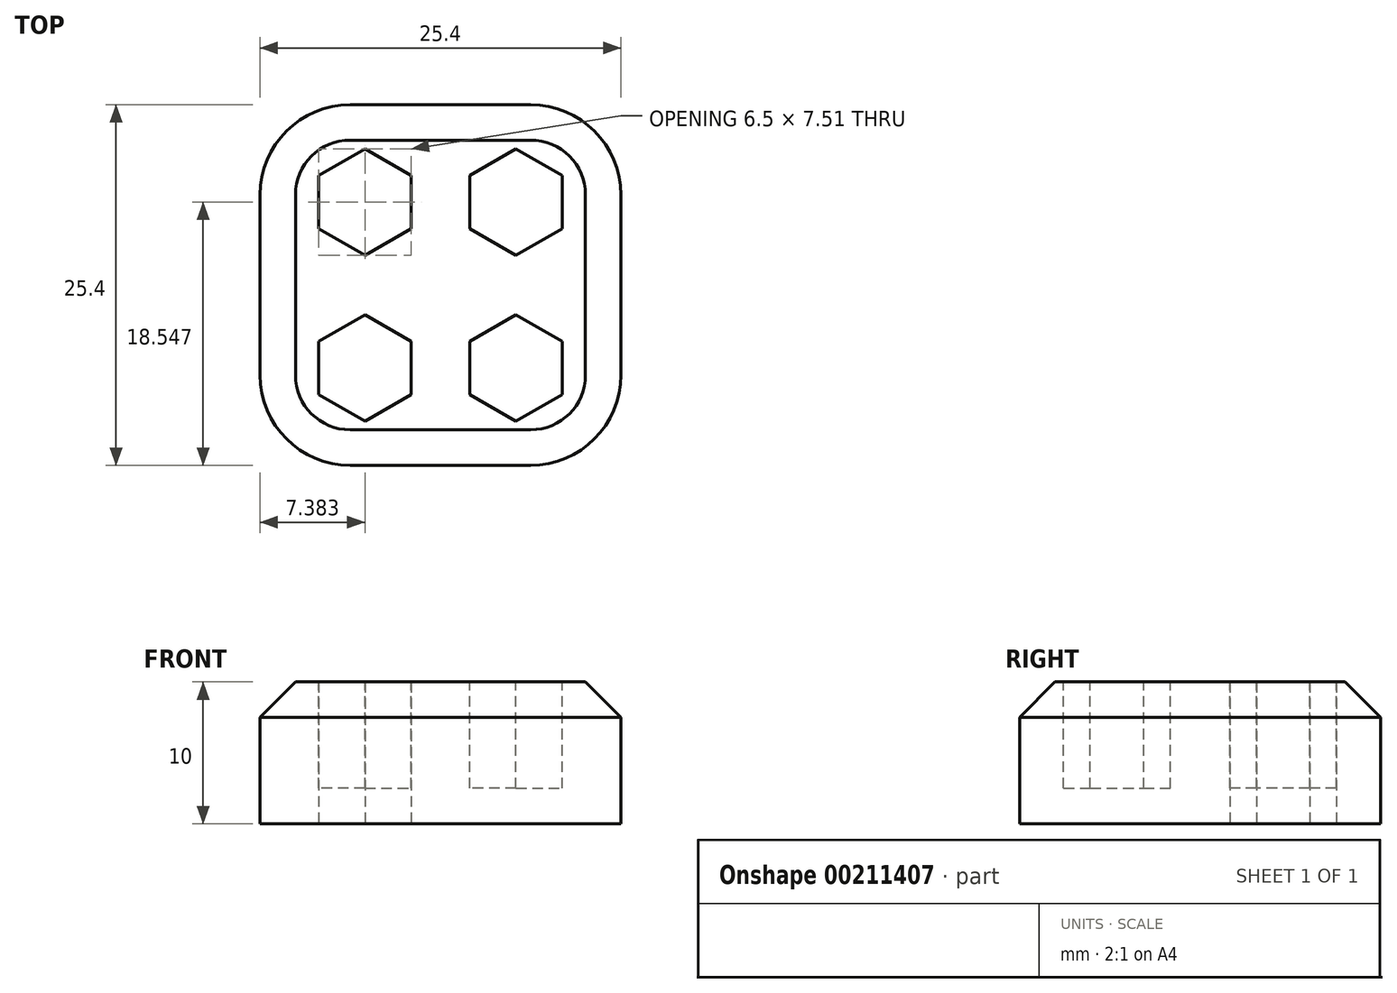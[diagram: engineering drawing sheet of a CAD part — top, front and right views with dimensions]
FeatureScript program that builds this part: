
annotation { "Feature Type Name" : "Feature", "Feature Type Description" : "" }
export const myFeature = defineFeature(function(context is Context, id is Id, definition is map)
    precondition{}
    {
        {
            var Q0;
            Q0=qCreatedBy(makeId("Top.planeOp"),FACE);
            var sketch = newSketch(context, id + "F0", { "sketchPlane" : qUnion([Q0])});
            skLineSegment(sketch, "E0.bottom", {"start": v(-12.7, 12.7) * mm, "end": v(12.7, 12.7) * mm});
            skLineSegment(sketch, "E0.top", {"start": v(-12.7, -12.7) * mm, "end": v(12.7, -12.7) * mm});
            skLineSegment(sketch, "E0.left", {"start": v(-12.7, 12.7) * mm, "end": v(-12.7, -12.7) * mm});
            skLineSegment(sketch, "E0.right", {"start": v(12.7, 12.7) * mm, "end": v(12.7, -12.7) * mm});
            skLineSegment(sketch, "E1", {"start": v(-12.7, 12.7) * mm, "end": v(12.7, -12.7) * mm, "construction": true});
            skLineSegment(sketch, "E2", {"start": v(-12.7, 5.85) * mm, "end": v(12.7, 5.85) * mm, "construction": true});
            skLineSegment(sketch, "E3", {"start": v(-5.32, 12.7) * mm, "end": v(-5.32, -12.7) * mm, "construction": true});
            skCircle(sketch, "E4.cCircle", {"center": v(-5.32, 5.85) * mm, "radius": 3.25 * mm, "construction": true});
            skLineSegment(sketch, "E4.0", {"start": v(-2.07, 7.72) * mm, "end": v(-2.07, 3.97) * mm});
            skLineSegment(sketch, "E4.1", {"start": v(-2.07, 3.97) * mm, "end": v(-5.32, 2.1) * mm});
            skLineSegment(sketch, "E4.2", {"start": v(-5.32, 2.1) * mm, "end": v(-8.57, 3.97) * mm});
            skLineSegment(sketch, "E4.3", {"start": v(-8.57, 3.97) * mm, "end": v(-8.57, 7.72) * mm});
            skLineSegment(sketch, "E4.4", {"start": v(-8.57, 7.72) * mm, "end": v(-5.32, 9.6) * mm});
            skLineSegment(sketch, "E4.5", {"start": v(-5.32, 9.6) * mm, "end": v(-2.07, 7.72) * mm});
            skPoint(sketch, "E4.0.midPoint", {"position": v(-2.07, 5.85) * mm});
            skCircle(sketch, "E5.MirrorC", {"center": v(5.32, 5.85) * mm, "radius": 3.25 * mm, "construction": true});
            skLineSegment(sketch, "E6.MirrorCS", {"start": v(2.07, 7.72) * mm, "end": v(2.07, 3.97) * mm});
            skLineSegment(sketch, "E7.MirrorCS", {"start": v(2.07, 3.97) * mm, "end": v(5.32, 2.1) * mm});
            skLineSegment(sketch, "E8.MirrorCS", {"start": v(5.32, 2.1) * mm, "end": v(8.57, 3.97) * mm});
            skLineSegment(sketch, "E9.MirrorCS", {"start": v(8.57, 3.97) * mm, "end": v(8.57, 7.72) * mm});
            skLineSegment(sketch, "E10.MirrorCS", {"start": v(5.32, 9.6) * mm, "end": v(2.07, 7.72) * mm});
            skLineSegment(sketch, "E11.MirrorCS", {"start": v(8.57, 7.72) * mm, "end": v(5.32, 9.6) * mm});
            skPoint(sketch, "E12.MirrorP", {"position": v(2.07, 5.85) * mm});
            skLineSegment(sketch, "E13.MirrorCS", {"start": v(8.57, -3.97) * mm, "end": v(8.57, -7.72) * mm});
            skPoint(sketch, "E14.MirrorP", {"position": v(-2.07, -5.85) * mm});
            skLineSegment(sketch, "E15.MirrorCS", {"start": v(5.32, -2.1) * mm, "end": v(8.57, -3.97) * mm});
            skCircle(sketch, "E16.MirrorC", {"center": v(-5.32, -5.85) * mm, "radius": 3.25 * mm, "construction": true});
            skLineSegment(sketch, "E17.MirrorCS", {"start": v(-2.07, -7.72) * mm, "end": v(-2.07, -3.97) * mm});
            skLineSegment(sketch, "E18.MirrorCS", {"start": v(-2.07, -3.97) * mm, "end": v(-5.32, -2.1) * mm});
            skLineSegment(sketch, "E19.MirrorCS", {"start": v(-5.32, -2.1) * mm, "end": v(-8.57, -3.97) * mm});
            skPoint(sketch, "E20.MirrorP", {"position": v(2.07, -5.85) * mm});
            skLineSegment(sketch, "E21.MirrorCS", {"start": v(2.07, -3.97) * mm, "end": v(5.32, -2.1) * mm});
            skLineSegment(sketch, "E22.MirrorCS", {"start": v(2.07, -7.72) * mm, "end": v(2.07, -3.97) * mm});
            skLineSegment(sketch, "E23.MirrorCS", {"start": v(-8.57, -3.97) * mm, "end": v(-8.57, -7.72) * mm});
            skLineSegment(sketch, "E24.MirrorCS", {"start": v(-5.32, -9.6) * mm, "end": v(-2.07, -7.72) * mm});
            skLineSegment(sketch, "E25.MirrorCS", {"start": v(8.57, -7.72) * mm, "end": v(5.32, -9.6) * mm});
            skLineSegment(sketch, "E26.MirrorCS", {"start": v(5.32, -9.6) * mm, "end": v(2.07, -7.72) * mm});
            skLineSegment(sketch, "E27.MirrorCS", {"start": v(-8.57, -7.72) * mm, "end": v(-5.32, -9.6) * mm});
            skCircle(sketch, "E28.MirrorC", {"center": v(5.32, -5.85) * mm, "radius": 3.25 * mm, "construction": true});
            skSolve(sketch);
        }
        {
            var Q0;
            Q0=makeQuery(id+"F0.imprint","IMPRINT",FACE,{"disambiguationData":[TD([[makeQuery(id+"F0.imprint","IMPRINT",EDGE,{"derivedFrom":sQuery(id+"F0.wireOp",EDGE,"E0.bottom")}),-1.0]])]});
            var Q1;
            Q1=makeQuery(id+"F0.imprint","IMPRINT",FACE,{"disambiguationData":[TD([[makeQuery(id+"F0.imprint","IMPRINT",EDGE,{"derivedFrom":sQuery(id+"F0.wireOp",EDGE,"E24.MirrorCS")}),1.0]])]});
            var Q2;
            Q2=makeQuery(id+"F0.imprint","IMPRINT",FACE,{"disambiguationData":[TD([[makeQuery(id+"F0.imprint","IMPRINT",EDGE,{"derivedFrom":sQuery(id+"F0.wireOp",EDGE,"E10.MirrorCS")}),1.0]])]});
            var Q3;
            Q3=makeQuery(id+"F0.imprint","IMPRINT",FACE,{"disambiguationData":[TD([[makeQuery(id+"F0.imprint","IMPRINT",EDGE,{"derivedFrom":sQuery(id+"F0.wireOp",EDGE,"E13.MirrorCS")}),-1.0]])]});
            var Q4;
            Q4=makeQuery(id+"F0.imprint","IMPRINT",FACE,{"disambiguationData":[TD([[makeQuery(id+"F0.imprint","IMPRINT",EDGE,{"derivedFrom":sQuery(id+"F0.wireOp",EDGE,"E4.5")}),-1.0]])]});
            extrude(context, id + "F1", {"entities" : qUnion([Q0, Q1, Q2, Q3, Q4]), "depth" : 10 * mm});
        }
        {
            var Q0;
            Q0=makeQuery(id+"F1.opExtrude","CAP_FACE",FACE,{"disambiguationData":[OSD([sQuery(id+"F0.wireOp",EDGE,"E0.bottom"),sQuery(id+"F0.wireOp",EDGE,"E0.top"),sQuery(id+"F0.wireOp",EDGE,"E0.left"),sQuery(id+"F0.wireOp",EDGE,"E0.right")])],"isStart":false});
            var sketch = newSketch(context, id + "F2", { "sketchPlane" : qUnion([Q0])});
            skLineSegment(sketch, "E29.0", {"start": v(-8.57, 7.72) * mm, "end": v(-5.32, 9.6) * mm});
            skLineSegment(sketch, "E30.0", {"start": v(-8.57, 3.97) * mm, "end": v(-8.57, 7.72) * mm});
            skLineSegment(sketch, "E31.0", {"start": v(-5.32, 2.1) * mm, "end": v(-8.57, 3.97) * mm});
            skLineSegment(sketch, "E32.0", {"start": v(-5.32, 9.6) * mm, "end": v(-2.07, 7.72) * mm});
            skLineSegment(sketch, "E33.0", {"start": v(-2.07, 7.72) * mm, "end": v(-2.07, 3.97) * mm});
            skLineSegment(sketch, "E34.0", {"start": v(-2.07, 3.97) * mm, "end": v(-5.32, 2.1) * mm});
            skLineSegment(sketch, "E35.MirrorCS", {"start": v(5.32, 2.1) * mm, "end": v(8.57, 3.97) * mm});
            skLineSegment(sketch, "E36.MirrorCS", {"start": v(5.32, 9.6) * mm, "end": v(2.07, 7.72) * mm});
            skLineSegment(sketch, "E37.MirrorCS", {"start": v(2.07, 7.72) * mm, "end": v(2.07, 3.97) * mm});
            skLineSegment(sketch, "E38.MirrorCS", {"start": v(2.07, 3.97) * mm, "end": v(5.32, 2.1) * mm});
            skLineSegment(sketch, "E39.MirrorCS", {"start": v(8.57, 7.72) * mm, "end": v(5.32, 9.6) * mm});
            skLineSegment(sketch, "E40.MirrorCS", {"start": v(8.57, 3.97) * mm, "end": v(8.57, 7.72) * mm});
            skLineSegment(sketch, "E41.MirrorCS", {"start": v(2.07, -3.97) * mm, "end": v(5.32, -2.1) * mm});
            skLineSegment(sketch, "E42.MirrorCS", {"start": v(2.07, -7.72) * mm, "end": v(2.07, -3.97) * mm});
            skLineSegment(sketch, "E43.MirrorCS", {"start": v(5.32, -9.6) * mm, "end": v(2.07, -7.72) * mm});
            skLineSegment(sketch, "E44.MirrorCS", {"start": v(-8.57, -3.97) * mm, "end": v(-8.57, -7.72) * mm});
            skLineSegment(sketch, "E45.MirrorCS", {"start": v(-8.57, -7.72) * mm, "end": v(-5.32, -9.6) * mm});
            skLineSegment(sketch, "E46.MirrorCS", {"start": v(-5.32, -2.1) * mm, "end": v(-8.57, -3.97) * mm});
            skLineSegment(sketch, "E47.MirrorCS", {"start": v(-5.32, -9.6) * mm, "end": v(-2.07, -7.72) * mm});
            skLineSegment(sketch, "E48.MirrorCS", {"start": v(-2.07, -7.72) * mm, "end": v(-2.07, -3.97) * mm});
            skLineSegment(sketch, "E49.MirrorCS", {"start": v(-2.07, -3.97) * mm, "end": v(-5.32, -2.1) * mm});
            skLineSegment(sketch, "E50.MirrorCS", {"start": v(5.32, -2.1) * mm, "end": v(8.57, -3.97) * mm});
            skLineSegment(sketch, "E51.MirrorCS", {"start": v(8.57, -7.72) * mm, "end": v(5.32, -9.6) * mm});
            skLineSegment(sketch, "E52.MirrorCS", {"start": v(8.57, -3.97) * mm, "end": v(8.57, -7.72) * mm});
            skSolve(sketch);
        }
        {
            var Q0;
            Q0 = qSketchRegion(id + "F2", true);
            extrude(context, id + "F3", {"entities" : qUnion([Q0]), "operationType" : NewBodyOperationType.REMOVE, "oppositeDirection" : true, "depth" : 7.5 * mm});
        }
        {
            var Q0;
            Q0=makeQuery(id+"F1.opExtrude","SWEPT_EDGE",EDGE,{"disambiguationData":[OSD([sQuery(id+"F0.wireOp",EDGE,"E0.top"),sQuery(id+"F0.wireOp",EDGE,"E0.left")])]});
            var Q1;
            Q1=makeQuery(id+"F1.opExtrude","SWEPT_EDGE",EDGE,{"disambiguationData":[OSD([sQuery(id+"F0.wireOp",EDGE,"E0.top"),sQuery(id+"F0.wireOp",EDGE,"E0.right")])]});
            var Q2;
            Q2=makeQuery(id+"F1.opExtrude","SWEPT_EDGE",EDGE,{"disambiguationData":[OSD([sQuery(id+"F0.wireOp",EDGE,"E0.bottom"),sQuery(id+"F0.wireOp",EDGE,"E0.right")])]});
            var Q3;
            Q3=makeQuery(id+"F1.opExtrude","SWEPT_EDGE",EDGE,{"disambiguationData":[OSD([sQuery(id+"F0.wireOp",EDGE,"E0.bottom"),sQuery(id+"F0.wireOp",EDGE,"E0.left")])]});
            fillet(context, id + "F4", {"entities" : qUnion([Q0, Q1, Q2, Q3]), "radius" : 6.35 * mm, "tangentPropagation" : true, "allowEdgeOverflow" : false});
        }
        {
            var Q0;
            Q0=makeQuery(id+"F1.opExtrude","CAP_EDGE",EDGE,{"disambiguationData":[OSD([sQuery(id+"F0.wireOp",EDGE,"E0.left")])],"isStart":false});
            var Q1;
            Q1=makeQuery(id+"F1.opExtrude","CAP_EDGE",EDGE,{"disambiguationData":[OSD([sQuery(id+"F0.wireOp",EDGE,"E0.top")])],"isStart":false});
            var Q2;
            Q2=makeQuery(id+"F1.opExtrude","CAP_EDGE",EDGE,{"disambiguationData":[OSD([sQuery(id+"F0.wireOp",EDGE,"E0.right")])],"isStart":false});
            var Q3;
            Q3=makeQuery(id+"F1.opExtrude","CAP_EDGE",EDGE,{"disambiguationData":[OSD([sQuery(id+"F0.wireOp",EDGE,"E0.bottom")])],"isStart":false});
            chamfer(context, id + "F5", {"entities" : qUnion([Q0, Q1, Q2, Q3]), "width" : 2.5 * mm, "tangentPropagation" : true});
        }
    });
